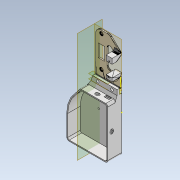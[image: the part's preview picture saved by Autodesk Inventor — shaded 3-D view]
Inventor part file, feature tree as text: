
AUTODESK INVENTOR PART (.ipt)
format: ipt  version: 2020.2 (Build 242310000, 310)  size: 4,601,344 bytes
history: native  units: in
note: dims shown in document units (in); Inventor stores cm internally (conversion verified against a paired STEP export)
features: extrude x18, sketch x17, thicken_offset x7, fillet x6, plane x4, other x2, split x2, projected_geometry x2, move_body x1, chamfer x1
ambient origin geometry x8: Origin, YZ Plane, XZ Plane, XY Plane, X Axis, Y Axis, Z Axis, Center Point
bodies: Solid1 (feature_tree), Solid2 (feature_tree), Solid3 (feature_tree)
feature tree (60):
  other  "ble_switch_mount"
  plane  "Work Plane1"
  other  "MeshFeature1"
  split  "Split1"
  extrude  "Extrusion1"  Depth=0.3937in TaperAngle=0.0deg
  extrude  "Extrusion3"  Depth=0.002in
  plane  "Work Plane2"
  extrude  "Extrusion4"  Depth=0.6299in TaperAngle=0.0deg
  thicken_offset  "Thicken1"
  fillet  "Fillet2"  Radius=4.5276in
  fillet  "Fillet3"  Radius=3.1496in
  extrude  "Extrusion5"  Depth=0.3937in
  plane  "Work Plane3"
  split  "Split3"
  move_body  "Move Body1"
  extrude  "Extrusion6"  Depth=2.3622in
  extrude  "Extrusion9"  Depth=0.8661in TaperAngle=0.0deg
  extrude  "Extrusion7"  TaperAngle=0.0deg  [1 undecoded]
  extrude  "Extrusion10"  Depth=0.0591in
  thicken_offset  "Thicken2"
  thicken_offset  "Thicken3"
  extrude  "Extrusion8"  TaperAngle=45.0deg  [1 undecoded]
  plane  "Work Plane4"
  thicken_offset  "Thicken4"
  sketch  "Sketch11"  dims[d39=0.3937in d40=1.9562in d41=0.0in]
  extrude  "Extrusion11"  Depth=0.3937in TaperAngle=0.0deg
  extrude  "Extrusion12"  Depth=0.3937in
  extrude  "Extrusion13"  Depth=0.3937in
  chamfer  "Chamfer2"  Distance=0.9681in
  thicken_offset  "Thicken5"
  thicken_offset  "Thicken6"
  thicken_offset  "Thicken7"
  fillet  "Fillet4"  Radius=0.3248in
  sketch  "Sketch13"  dims[d44=0.3937in d45=0.1969in]
  sketch  "Sketch14"  dims[d46=0.1969in d47=0.9681in d48=0.0in d50=0.3248in]
  sketch  "Sketch15"  dims[d51=0.3937in d55=0.3248in]
  sketch  "Sketch16"  dims[d56=0.3937in d57=0.0984in d58=0.0in]
  extrude  "Extrusion15"  Depth=0.3937in
  extrude  "Extrusion16"  Depth=0.3937in TaperAngle=0.0deg
  extrude  "Extrusion17"  Depth=1.624in TaperAngle=0.0deg
  extrude  "Extrusion18"  Depth=0.0787in
  fillet  "Fillet6"  Radius=0.0394in
  fillet  "Fillet7"  Radius=0.0394in
  extrude  "Extrusion19"  Depth=0.0787in
  extrude  "Extrusion20"  Depth=0.0787in
  fillet  "Fillet8"  Radius=0.0197in
  sketch  "Sketch2"  dims[d1=0.002in d3=0.3937in d4=0.0in]
  sketch  "Sketch3"  dims[d5=0.002in d6=0.002in]
  sketch  "Sketch4"  dims[d7=0.002in d10=0.6299in d11=0.0in d12=4.5276in d13=3.1496in]
  sketch  "Sketch5"  dims[d15=0.3937in d16=0.0in d17=0.2953in d18=0.2953in]
  sketch  "Sketch6"  dims[d19=1.5748in d26=2.3622in d27=2.3622in]
  sketch  "Sketch7"  dims[d28=0.1969in d29=0.8661in d30=0.0in]
  sketch  "Sketch8"  dims[d31=0.3543in d32=0.0in d33=-0.0197in d34=0.0in]
  sketch  "Sketch9"  dims[d35=0.374in d36=0.0591in]
  sketch  "Sketch10"  dims[d37=0.189in d38=45.0deg]
  sketch  "Sketch12"  dims[d42=0.2165in d43=0.3937in]
  projected_geometry  "Projected Loop1"
  projected_geometry  "Projected Loop2"
  sketch  "Sketch17"  dims[d59=0.0197in d60=0.0in d61=1.624in d62=0.0in]
  sketch  "Sketch18"  dims[d63=0.0in d64=0.0394in d65=0.0394in d66=0.0394in d67=0.0394in d68=0.0197in d69=0.0197in d70=0.0003in d71=0.0in d72=0.3937in d73=0.0in d74=0.0787in d75=0.9562in d76=0.0in d77=0.3504in d78=0.0787in d79=45.0deg d83=0.0197in d84=0.0197in d85=0.3937in d86=0.0197in d87=0.7874in d88=0.7874in d89=0.1575in d94=0.1083in d95=0.0787in d96=0.2953in d97=0.9429in d98=0.0787in d99=0.1083in d100=0.2953in d101=0.7965in d102=0.1083in d103=0.0787in d104=0.2953in d105=1.378in d106=0.1083in d107=0.0787in d108=0.2953in d109=1.7807in d110=0.0472in d111=0.0in d112=0.0472in d113=0.0in d114=0.0472in d115=0.0in d116=0.0472in d117=0.0in d118=0.0591in d119=0.0433in d120=0.0433in d121=0.0591in d122=0.9562in d123=0.0in d124=0.3937in d125=0.0in d126=0.0787in]
note: 2 required parameter values undecoded (feature->parameter linkage not recoverable at this tier; creation-order binding heuristic only, values carry confidence <= 0.55)
